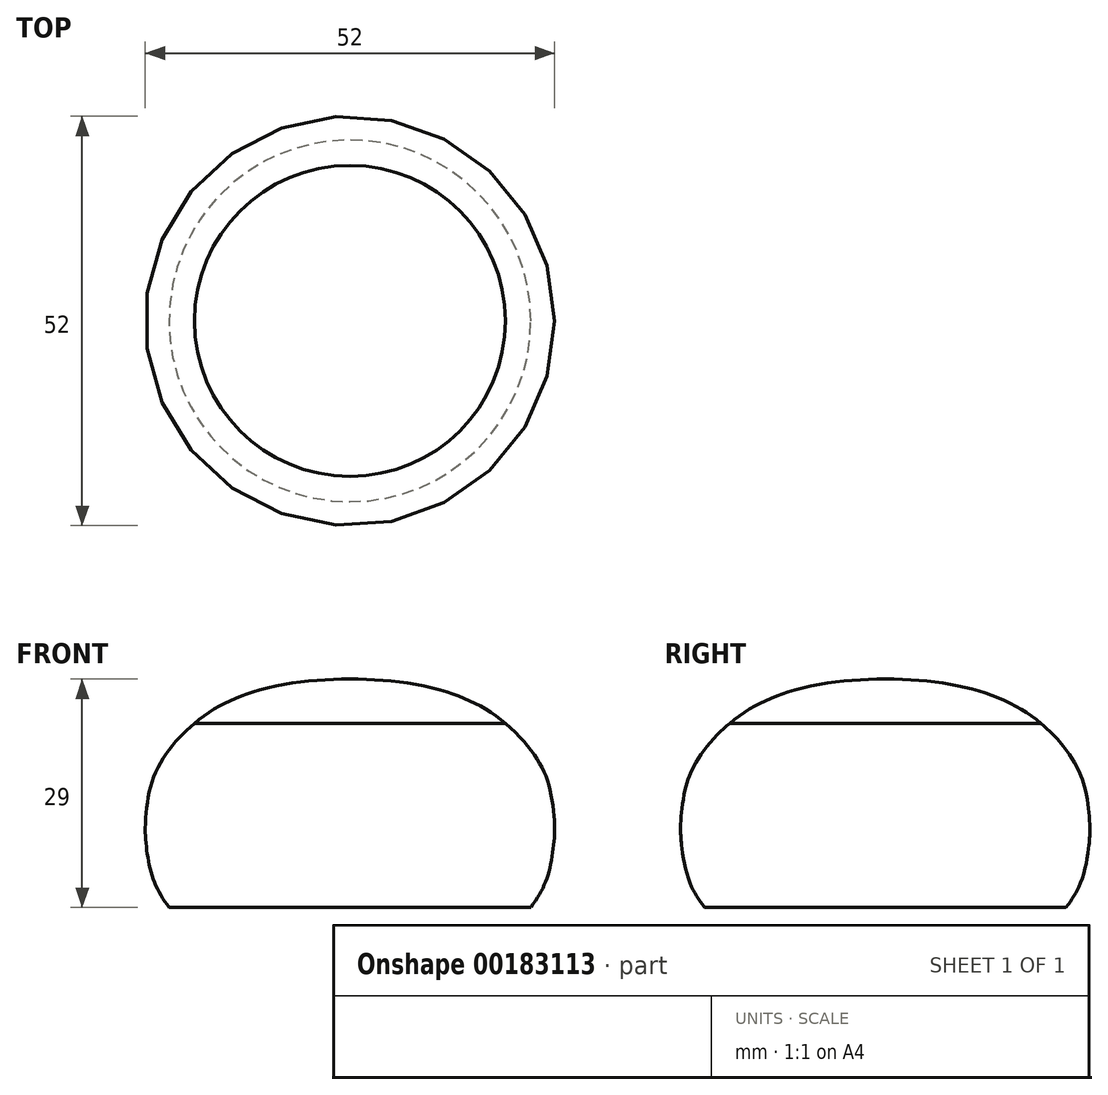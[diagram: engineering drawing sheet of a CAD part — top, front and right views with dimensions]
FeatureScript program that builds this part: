
annotation { "Feature Type Name" : "Feature", "Feature Type Description" : "" }
export const myFeature = defineFeature(function(context is Context, id is Id, definition is map)
    precondition{}
    {
        {
            var Q0;
            Q0=qCreatedBy(makeId("Right.planeOp"),FACE);
            var sketch = newSketch(context, id + "F0", { "sketchPlane" : qUnion([Q0])});
            skFitSpline(sketch, "E0", {"points": [v(0, 19) * mm, v(16.5, 15.6) * mm, v(23.3, 9.56) * mm, v(25.4, 5) * mm, v(26, 0) * mm], "startDerivative": vector(55.77, 0) * mm, "endDerivative": vector(0, -18.91) * mm});
            skFitSpline(sketch, "E1.MirrorCS", {"points": [v(0, 19) * mm, v(-16.5, 15.6) * mm, v(-23.3, 9.56) * mm, v(-25.4, 5) * mm, v(-26, 0) * mm], "startDerivative": vector(-55.77, 0) * mm, "endDerivative": vector(0, -18.91) * mm, "construction": true});
            skFitSpline(sketch, "E2.MirrorCS", {"points": [v(0, -19) * mm, v(-16.5, -15.6) * mm, v(-23.3, -9.56) * mm, v(-25.4, -5) * mm, v(-26, 0) * mm], "startDerivative": vector(-55.77, 0) * mm, "endDerivative": vector(0, 18.91) * mm, "construction": true});
            skFitSpline(sketch, "E3.MirrorCS", {"points": [v(0, -19) * mm, v(16.5, -15.6) * mm, v(23.3, -9.56) * mm, v(25.4, -5) * mm, v(26, 0) * mm], "startDerivative": vector(55.77, 0) * mm, "endDerivative": vector(0, 18.91) * mm});
            skLineSegment(sketch, "E4", {"start": v(0, 19) * mm, "end": v(0, -19) * mm});
            skLineSegment(sketch, "E5", {"start": v(19.75, 13.38) * mm, "end": v(0, 13.38) * mm});
            skSolve(sketch);
        }
        {
            var Q0;
            {var subQ0=sQuery(id+"F0.wireOp",EDGE,"E3.MirrorCS");Q0=makeQuery(id+"F0.imprint","IMPRINT",FACE,{"disambiguationData":[TD([[makeQuery(id+"F0.imprint","IMPRINT",EDGE,{"derivedFrom":subQ0}),1.0]])]});}
            var Q1;
            Q1=sQuery(id+"F0.wireOp",EDGE,"E4");
            revolve(context, id + "F1", {"entities" : qUnion([Q0]), "axis" : qUnion([Q1]), "revolveType" : RevolveType.FULL});
        }
        {
            var Q0;
            {var subQ3=sQuery(id+"F0.wireOp",EDGE,"E5");Q0=makeQuery(id+"F0.imprint","IMPRINT",FACE,{"disambiguationData":[TD([[makeQuery(id+"F0.imprint","IMPRINT",EDGE,{"derivedFrom":subQ3}),-1.0]])]});}
            var Q1;
            Q1=sQuery(id+"F0.wireOp",EDGE,"E4");
            revolve(context, id + "F2", {"entities" : qUnion([Q0]), "axis" : qUnion([Q1]), "revolveType" : RevolveType.FULL});
        }
        {
            var Q0;
            Q0=qCreatedBy(makeId("Right.planeOp"),FACE);
            var sketch = newSketch(context, id + "F3", { "sketchPlane" : qUnion([Q0])});
            skLineSegment(sketch, "E6.bottom", {"start": v(-42.44, -10) * mm, "end": v(53.33, -10) * mm});
            skLineSegment(sketch, "E6.top", {"start": v(-42.44, -57.54) * mm, "end": v(53.33, -57.54) * mm});
            skLineSegment(sketch, "E6.left", {"start": v(-42.44, -10) * mm, "end": v(-42.44, -57.54) * mm});
            skLineSegment(sketch, "E6.right", {"start": v(53.33, -10) * mm, "end": v(53.33, -57.54) * mm});
            skSolve(sketch);
        }
        {
            var Q0;
            Q0=makeQuery(id+"F3.imprint","IMPRINT",FACE,{"disambiguationData":[TD([[makeQuery(id+"F3.imprint","IMPRINT",EDGE,{"derivedFrom":sQuery(id+"F3.wireOp",EDGE,"E6.bottom")}),-1.0]])]});
            extrude(context, id + "F4", {"entities" : qUnion([Q0]), "operationType" : NewBodyOperationType.REMOVE, "oppositeDirection" : true, "depth" : 50 * mm, "symmetric" : true});
        }
    });
